# Revit family: Furniture_ShelvingStorage_Sjobergs_Cabinet_2
name_source: partatom
category: Furniture
revit_build: Autodesk Revit 2018 (Build: 20170223_1515(x64)
units: mm (PartAtom-declared; Revit-internal decimal feet)

## family parameters
Always vertical = Yes
Cut with Voids When Loaded = No
OmniClass Number = 23.40.20.27.21
OmniClass Title = Mobile Storage Units
Room Calculation Point = No
Shared = No
Work Plane-Based = No

## types (1)
- 33031 Sjobergs Complete Cabinet 2
    AssetType = Movable
    BIMObjectName = Furniture_Shelving&Storage_Sjobergs_Cabinet_2
    Brand = Sjobergs
    Category = Cabinets
    Collection = Cabinet
    Color = Wooden
    ConvergoRefNr = 0184-2005-0012-SE
    Cost = 0 $
    Description = A full height cabinet includes three fixed and four removable shelves.
    DrawerTertiaryMaterial = Clearance
    Features = As stable, robust and functional as Cabinet 1 with half-doors in birch and potty hinges that allow the doors to open 170 degrees.
The interior consists of 4 fixed and 4 removable shelves in 18 mm birch plywood.
With base, the cabinet has a full height of 2100 mm, depth 490 mm and width of
1000 mm.
A sturdy cabinet for student work or other storage. Frame and interior in 18
mm birch plywood that provides both stability and durability. Doors in birch.
The cabinets come unmounted in flat pack, knock down. Everything to minimize
the risk of injury during transport. The mounting of the cabinets is very simple,
installation instructions are included in the packages.
We also supply pre-assembled cabinets at an additional cost.
    Finish = Birch plywood 18 mm, doors in birch laminate
    IfcExportAs = IfcFurnitureType
    IfcExportType = DRAWER
    MainColor = Wooden
    ManufacterURL = https://www.sjobergs.se
    Manufacturer = Sjobergs
    ManufacturerName = Sjobergs
    Material = Wood
    Model = 33031 Sjobergs Complete Cabinet 2
    ModelNumber = 33031
    NBSDescription = Cabinets
    NBSReference = 45-35-47/415
    Name = Sjobergs_Cabinet_2
    NominalDepth = 930 mm
    NominalHeight = 2100 mm
    NominalWidth = 1000 mm  [stored 3.28084 ft]
    ProductDatasheet = https://www.sjobergs.se
    ProductInformation = A full height cabinet includes three fixed and four removable shelves.
    Shape = Sculptured
    Size = 1000x490x2100 mm
    URL = https://www.sjobergs.se
    Uniclass2 = Pr_40_30_78_24
    Uniclass2015Description = Storage units
    Uniclass2015Reference = Pr_40_30_78_25
    Version = 1
    VersionDate = 30/06/2020

note: [stored X ft] marks values corroborated as IEEE doubles in the binary element streams (Revit-internal decimal feet)

## geometry (parser evidence)
native form markers: Sweep x5
no freeform markers — native parametric forms only
